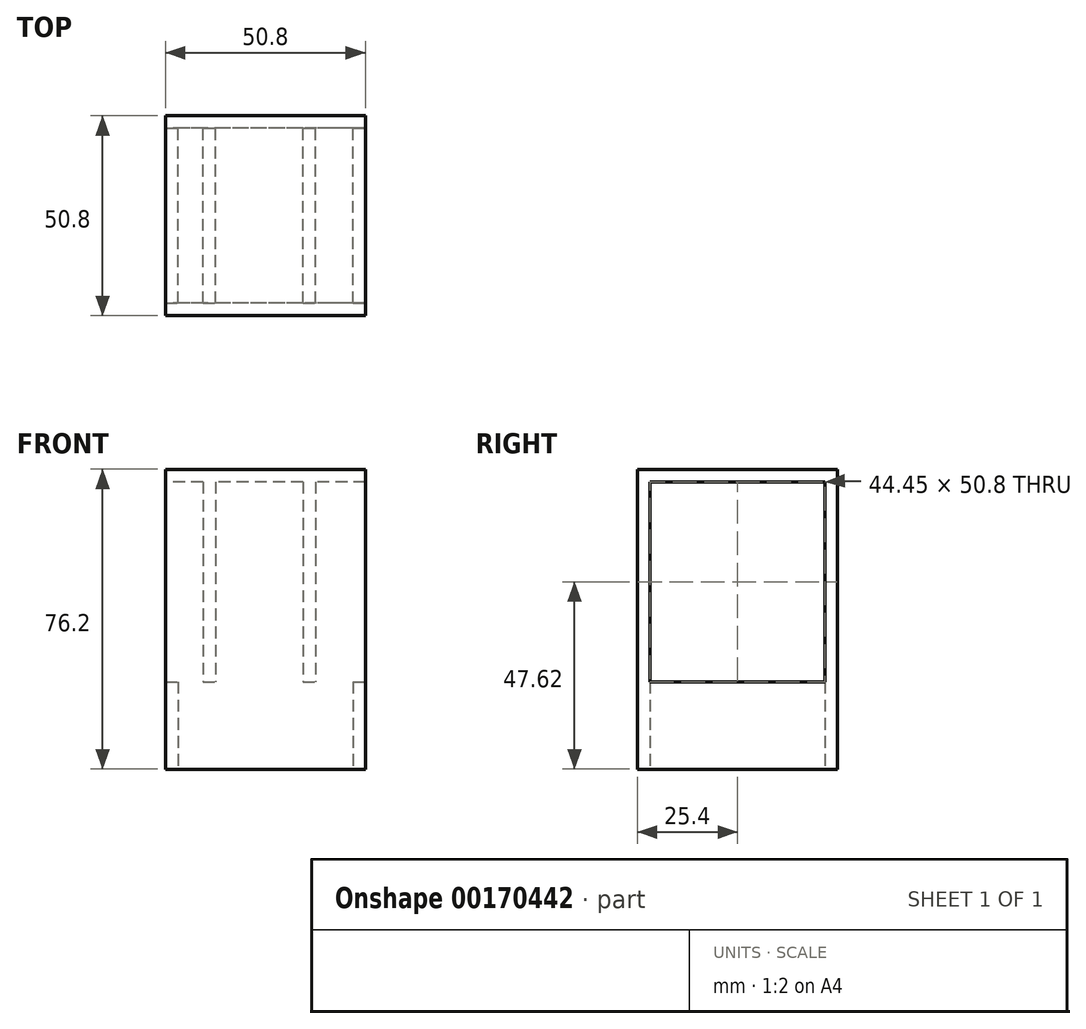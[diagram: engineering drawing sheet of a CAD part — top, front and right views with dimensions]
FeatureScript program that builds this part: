
annotation { "Feature Type Name" : "Feature", "Feature Type Description" : "" }
export const myFeature = defineFeature(function(context is Context, id is Id, definition is map)
    precondition{}
    {
        {
            var Q0;
            Q0=qCreatedBy(makeId("Front.planeOp"),FACE);
            var sketch = newSketch(context, id + "F0", { "sketchPlane" : qUnion([Q0])});
            skLineSegment(sketch, "E0.bottom", {"start": v(0, 25.4) * mm, "end": v(0, 25.4) * mm});
            skLineSegment(sketch, "E0.top", {"start": v(0, -25.4) * mm, "end": v(0, -25.4) * mm});
            skLineSegment(sketch, "E0.left", {"start": v(0, 25.4) * mm, "end": v(0, -25.4) * mm});
            skLineSegment(sketch, "E0.right", {"start": v(0, 25.4) * mm, "end": v(0, -25.4) * mm});
            skPoint(sketch, "E0.middle", {"position": v(0, 0) * mm});
            skLineSegment(sketch, "E1.bottom", {"start": v(-15.87, 25.4) * mm, "end": v(-12.7, 25.4) * mm});
            skLineSegment(sketch, "E2.bottom", {"start": v(9.53, 25.4) * mm, "end": v(12.7, 25.4) * mm});
            skLineSegment(sketch, "E2.top", {"start": v(9.53, -25.4) * mm, "end": v(12.7, -25.4) * mm});
            skLineSegment(sketch, "E2.left", {"start": v(9.53, 25.4) * mm, "end": v(9.53, -25.4) * mm});
            skLineSegment(sketch, "E2.right", {"start": v(12.7, 25.4) * mm, "end": v(12.7, -25.4) * mm});
            skPoint(sketch, "E2.middle", {"position": v(11.11, 0) * mm});
            skLineSegment(sketch, "E3.bottom", {"start": v(25.4, 25.4) * mm, "end": v(-25.4, 25.4) * mm});
            skLineSegment(sketch, "E3.top", {"start": v(25.4, 28.58) * mm, "end": v(-25.4, 28.58) * mm});
            skLineSegment(sketch, "E3.left", {"start": v(25.4, 25.4) * mm, "end": v(25.4, 28.58) * mm});
            skLineSegment(sketch, "E3.right", {"start": v(-25.4, 25.4) * mm, "end": v(-25.4, 28.58) * mm});
            skPoint(sketch, "E3.middle", {"position": v(0, 26.99) * mm});
            skLineSegment(sketch, "E4.bottom", {"start": v(25.4, 25.4) * mm, "end": v(25.4, 25.4) * mm});
            skLineSegment(sketch, "E4.right", {"start": v(25.4, 25.4) * mm, "end": v(25.4, -38.7) * mm});
            skLineSegment(sketch, "E5.bottom", {"start": v(-25.4, 25.4) * mm, "end": v(-22.23, 25.4) * mm});
            skLineSegment(sketch, "E5.top", {"start": v(-25.4, -25.4) * mm, "end": v(-22.23, -25.4) * mm});
            skLineSegment(sketch, "E5.left", {"start": v(-25.4, 25.4) * mm, "end": v(-25.4, -25.4) * mm});
            skLineSegment(sketch, "E5.right", {"start": v(-22.23, 25.4) * mm, "end": v(-22.23, -25.4) * mm});
            skPoint(sketch, "E5.middle", {"position": v(-23.81, 0) * mm});
            skLineSegment(sketch, "E6.bottom", {"start": v(-25.4, -25.4) * mm, "end": v(25.4, -25.4) * mm});
            skLineSegment(sketch, "E6.left", {"start": v(-25.4, -25.4) * mm, "end": v(-25.4, -47.62) * mm});
            skLineSegment(sketch, "E6.right", {"start": v(25.4, -25.4) * mm, "end": v(25.4, -47.62) * mm});
            skLineSegment(sketch, "E7.left", {"start": v(25.4, 31.63) * mm, "end": v(25.4, -31.63) * mm});
            skLineSegment(sketch, "E8.bottom", {"start": v(25.4, 25.4) * mm, "end": v(19.48, 25.4) * mm});
            skLineSegment(sketch, "E8.left", {"start": v(25.4, 25.4) * mm, "end": v(25.4, -39.36) * mm});
            skLineSegment(sketch, "E9.bottom", {"start": v(25.4, 25.4) * mm, "end": v(22.23, 25.4) * mm});
            skLineSegment(sketch, "E9.top", {"start": v(25.4, -25.4) * mm, "end": v(22.23, -25.4) * mm});
            skLineSegment(sketch, "E9.left", {"start": v(25.4, 25.4) * mm, "end": v(25.4, -25.4) * mm});
            skLineSegment(sketch, "E9.right", {"start": v(22.23, 25.4) * mm, "end": v(22.23, -25.4) * mm});
            skPoint(sketch, "E9.middle", {"position": v(23.81, 0) * mm});
            skLineSegment(sketch, "E10", {"start": v(-3.18, 25.4) * mm, "end": v(-3.18, -25.4) * mm});
            skLineSegment(sketch, "E11", {"start": v(-12.7, 25.4) * mm, "end": v(-12.7, -25.4) * mm});
            skLineSegment(sketch, "E12", {"start": v(-22.23, -25.4) * mm, "end": v(-22.23, -47.63) * mm});
            skLineSegment(sketch, "E13", {"start": v(22.23, -25.4) * mm, "end": v(22.23, -47.63) * mm});
            skLineSegment(sketch, "E14", {"start": v(-15.87, 25.4) * mm, "end": v(-15.87, -25.4) * mm});
            skLineSegment(sketch, "E15", {"start": v(-22.23, -47.63) * mm, "end": v(-22.23, -47.62) * mm});
            skLineSegment(sketch, "E16", {"start": v(22.23, -47.63) * mm, "end": v(22.23, -47.62) * mm});
            skLineSegment(sketch, "E17", {"start": v(-22.23, -47.62) * mm, "end": v(-25.4, -47.62) * mm});
            skLineSegment(sketch, "E18", {"start": v(25.4, -47.62) * mm, "end": v(22.23, -47.62) * mm});
            skSolve(sketch);
        }
        {
            var Q0;
            Q0=makeQuery(id+"F0.imprint","IMPRINT",FACE,{"disambiguationData":[TD([[makeQuery(id+"F0.imprint","IMPRINT",EDGE,{"derivedFrom":sQuery(id+"F0.wireOp",EDGE,"E3.top")}),1.0]])]});
            var Q1;
            Q1=makeQuery(id+"F0.imprint","IMPRINT",FACE,{"disambiguationData":[TD([[makeQuery(id+"F0.imprint","IMPRINT",EDGE,{"derivedFrom":sQuery(id+"F0.wireOp",EDGE,"E5.bottom")}),-1.0]])]});
            var Q2;
            {var subQ0=sQuery(id+"F0.wireOp",EDGE,"E11");Q2=makeQuery(id+"F0.imprint","IMPRINT",FACE,{"disambiguationData":[TD([[makeQuery(id+"F0.imprint","IMPRINT",EDGE,{"derivedFrom":subQ0}),-1.0]])]});}
            var Q3;
            {var subQ0=sQuery(id+"F0.wireOp",EDGE,"E9.bottom");Q3=makeQuery(id+"F0.imprint","IMPRINT",FACE,{"disambiguationData":[TD([[makeQuery(id+"F0.imprint","IMPRINT",EDGE,{"derivedFrom":subQ0}),1.0]])]});}
            var Q4;
            {var subQ0=sQuery(id+"F0.wireOp",EDGE,"E2.left");Q4=makeQuery(id+"F0.imprint","IMPRINT",FACE,{"disambiguationData":[TD([[makeQuery(id+"F0.imprint","IMPRINT",EDGE,{"derivedFrom":subQ0}),1.0]])]});}
            var Q5;
            {var subQ0=sQuery(id+"F0.wireOp",EDGE,"E0.right");Q5=makeQuery(id+"F0.imprint","IMPRINT",FACE,{"disambiguationData":[TD([[makeQuery(id+"F0.imprint","IMPRINT",EDGE,{"derivedFrom":subQ0}),-1.0]])]});}
            var Q6;
            Q6=makeQuery(id+"F0.imprint","IMPRINT",FACE,{"disambiguationData":[TD([[makeQuery(id+"F0.imprint","IMPRINT",EDGE,{"derivedFrom":sQuery(id+"F0.wireOp",EDGE,"E6.top")}),1.0]])]});
            var Q7;
            {var subQ2=sQuery(id+"F0.wireOp",EDGE,"E6.right");Q7=makeQuery(id+"F0.imprint","IMPRINT",FACE,{"disambiguationData":[TD([[makeQuery(id+"F0.imprint","IMPRINT",EDGE,{"derivedFrom":subQ2}),-1.0]])]});}
            var Q8;
            {var subQ0=sQuery(id+"F0.wireOp",EDGE,"E6.left");Q8=makeQuery(id+"F0.imprint","IMPRINT",FACE,{"disambiguationData":[TD([[makeQuery(id+"F0.imprint","IMPRINT",EDGE,{"derivedFrom":subQ0}),1.0]])]});}
            extrude(context, id + "F1", {"entities" : qUnion([Q0, Q1, Q2, Q3, Q4, Q5, Q6, Q7, Q8]), "endBound" : BoundingType.SYMMETRIC, "depth" : 44.45 * mm});
        }
        {
            var Q0;
            Q0=qCreatedBy(makeId("Right.planeOp"),FACE);
            var sketch = newSketch(context, id + "F2", { "sketchPlane" : qUnion([Q0])});
            skLineSegment(sketch, "E19.bottom", {"start": v(-22.23, 28.58) * mm, "end": v(-25.4, 28.58) * mm});
            skLineSegment(sketch, "E19.top", {"start": v(-22.22, -47.62) * mm, "end": v(-25.4, -47.62) * mm});
            skLineSegment(sketch, "E19.left", {"start": v(-22.23, 28.58) * mm, "end": v(-22.22, -47.62) * mm});
            skLineSegment(sketch, "E19.right", {"start": v(-25.4, 28.58) * mm, "end": v(-25.4, -47.62) * mm});
            skLineSegment(sketch, "E20.bottom", {"start": v(22.22, 28.57) * mm, "end": v(25.4, 28.57) * mm});
            skLineSegment(sketch, "E20.top", {"start": v(22.23, -47.63) * mm, "end": v(25.4, -47.63) * mm});
            skLineSegment(sketch, "E20.left", {"start": v(22.22, 28.57) * mm, "end": v(22.23, -47.63) * mm});
            skLineSegment(sketch, "E20.right", {"start": v(25.4, 28.57) * mm, "end": v(25.4, -47.63) * mm});
            skSolve(sketch);
        }
        {
            var Q0;
            Q0=makeQuery(id+"F2.imprint","IMPRINT",FACE,{"disambiguationData":[TD([[makeQuery(id+"F2.imprint","IMPRINT",EDGE,{"derivedFrom":sQuery(id+"F2.wireOp",EDGE,"E19.bottom")}),1.0]])]});
            var Q1;
            Q1=makeQuery(id+"F2.imprint","IMPRINT",FACE,{"disambiguationData":[TD([[makeQuery(id+"F2.imprint","IMPRINT",EDGE,{"derivedFrom":sQuery(id+"F2.wireOp",EDGE,"E20.bottom")}),-1.0]])]});
            extrude(context, id + "F3", {"entities" : qUnion([Q0, Q1]), "operationType" : NewBodyOperationType.ADD, "endBound" : BoundingType.SYMMETRIC, "depth" : 50.8 * mm});
        }
    });
